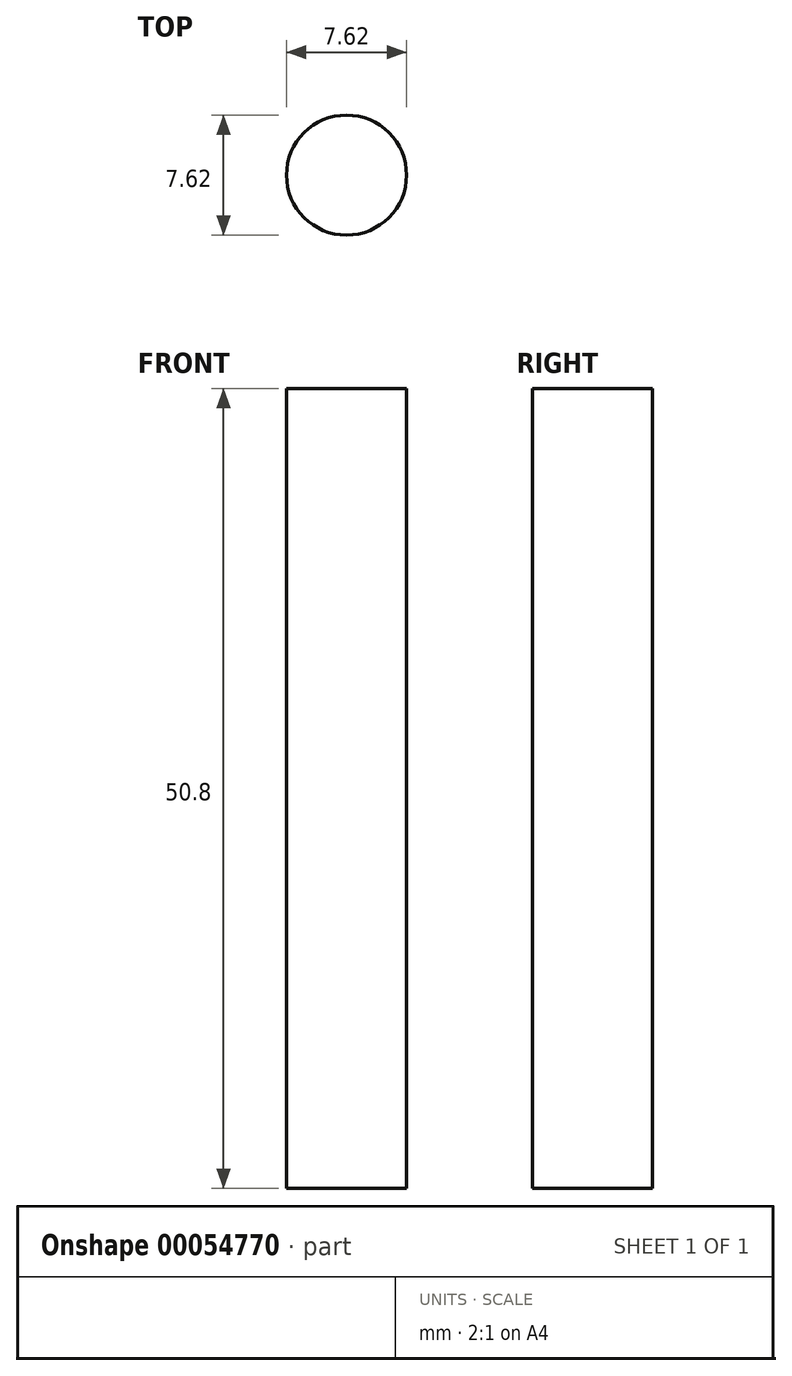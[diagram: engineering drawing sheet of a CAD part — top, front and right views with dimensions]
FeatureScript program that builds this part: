
annotation { "Feature Type Name" : "Feature", "Feature Type Description" : "" }
export const myFeature = defineFeature(function(context is Context, id is Id, definition is map)
    precondition{}
    {
        {
            var Q0;
            Q0=qCreatedBy(makeId("Top.planeOp"),FACE);
            var sketch = newSketch(context, id + "F0", { "sketchPlane" : qUnion([Q0])});
            skCircle(sketch, "E0", {"center": v(0, 0) * mm, "radius": 3.81 * mm});
            skSolve(sketch);
        }
        {
            var Q0;
            Q0=makeQuery(id+"F0.imprint","IMPRINT",FACE,{"disambiguationData":[TD([[makeQuery(id+"F0.imprint","IMPRINT",EDGE,{"derivedFrom":sQuery(id+"F0.wireOp",EDGE,"E0")}),1.0]])]});
            extrude(context, id + "F1", {"entities" : qUnion([Q0]), "depth" : 50.8 * mm});
        }
    });
